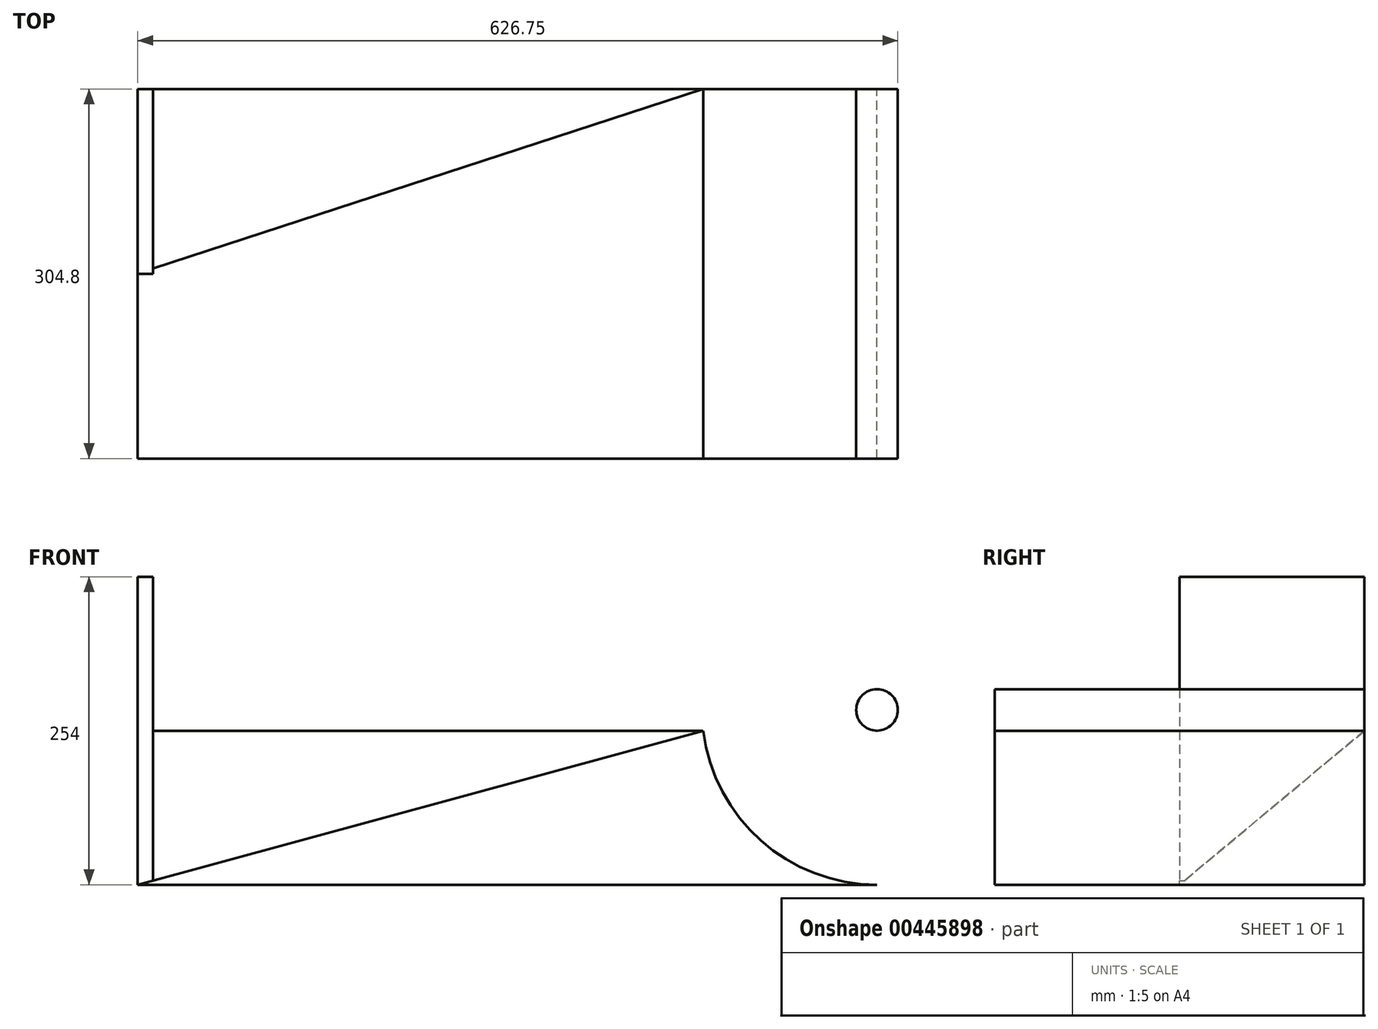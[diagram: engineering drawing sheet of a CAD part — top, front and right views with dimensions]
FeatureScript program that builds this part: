
annotation { "Feature Type Name" : "Feature", "Feature Type Description" : "" }
export const myFeature = defineFeature(function(context is Context, id is Id, definition is map)
    precondition{}
    {
        {
            var Q0;
            Q0=qCreatedBy(makeId("Front.planeOp"),FACE);
            var sketch = newSketch(context, id + "F0", { "sketchPlane" : qUnion([Q0])});
            skArc(sketch, "E0", {"start": v(-143.12, -17.15) * mm, "mid": v(-95.67, -107.82) * mm, "end": v(0, -144.15) * mm});
            skLineSegment(sketch, "E1", {"start": v(0, 0) * mm, "end": v(0, -144.15) * mm});
            skLineSegment(sketch, "E2", {"start": v(0, -144.15) * mm, "end": v(-609.6, -144.15) * mm});
            skLineSegment(sketch, "E3", {"start": v(-143.12, -17.15) * mm, "end": v(-143.12, -144.15) * mm});
            skLineSegment(sketch, "E4", {"start": v(-143.12, -17.15) * mm, "end": v(-609.6, -144.15) * mm});
            skCircle(sketch, "E5", {"center": v(0, 0) * mm, "radius": 17.15 * mm});
            skSolve(sketch);
        }
        {
            var Q0;
            Q0 = qSketchRegion(id + "F0", true);
            extrude(context, id + "F1", {"entities" : qUnion([Q0]), "depth" : 304.8 * mm});
        }
        {
            var Q0;
            Q0=makeQuery(id+"F1.opExtrude","SWEPT_FACE",FACE,{"disambiguationData":[OSD([sQuery(id+"F0.wireOp",EDGE,"E2")])]});
            var sketch = newSketch(context, id + "F2", { "sketchPlane" : qUnion([Q0])});
            skLineSegment(sketch, "E6", {"start": v(-609.6, 152.4) * mm, "end": v(-596.9, 152.4) * mm});
            skLineSegment(sketch, "E7", {"start": v(-596.9, 152.4) * mm, "end": v(-596.9, 0) * mm});
            skLineSegment(sketch, "E8", {"start": v(-596.9, 0) * mm, "end": v(-609.6, 0) * mm});
            skLineSegment(sketch, "E9", {"start": v(-609.6, 0) * mm, "end": v(-609.6, 152.4) * mm});
            skSolve(sketch);
        }
        {
            var Q0;
            Q0 = qSketchRegion(id + "F2", true);
            extrude(context, id + "F3", {"entities" : qUnion([Q0]), "operationType" : NewBodyOperationType.ADD, "oppositeDirection" : true, "depth" : 254 * mm});
        }
        {
            var Q0;
            Q0=makeQuery(id+"F3.opExtrude","SWEPT_FACE",FACE,{"disambiguationData":[OSD([sQuery(id+"F2.wireOp",EDGE,"E9")])]});
            var sketch = newSketch(context, id + "F4", { "sketchPlane" : qUnion([Q0])});
            skLineSegment(sketch, "E10", {"start": v(0, -17.15) * mm, "end": v(152.4, -144.15) * mm});
            skLineSegment(sketch, "E11", {"start": v(152.4, -144.15) * mm, "end": v(0, -144.15) * mm});
            skLineSegment(sketch, "E12", {"start": v(0, -144.15) * mm, "end": v(0, -17.15) * mm});
            skSolve(sketch);
        }
        {
            var Q0;
            Q0 = qSketchRegion(id + "F4", true);
            extrude(context, id + "F5", {"entities" : qUnion([Q0]), "operationType" : NewBodyOperationType.ADD, "oppositeDirection" : true, "depth" : 466.1 * mm});
        }
    });
